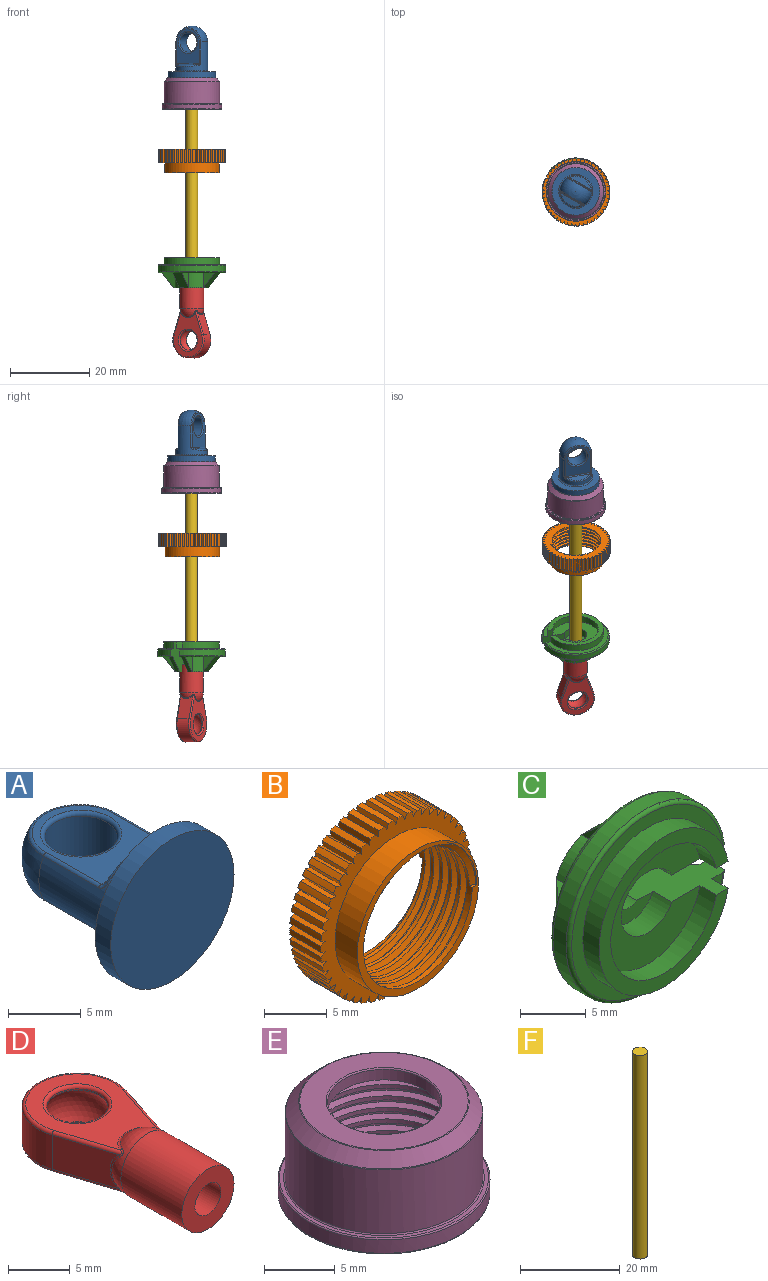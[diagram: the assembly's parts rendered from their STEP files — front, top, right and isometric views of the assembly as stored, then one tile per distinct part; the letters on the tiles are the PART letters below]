
ASSEMBLY  parts=6 mates=5
PART A: 27 faces, bbox 12x13x12 mm
  f0: revolved ~8x8mm, area 46.2mm2, adj f2,f6,f13
  f1: plane 8.65x6.57mm, normal (0,0,-1), area 27.5mm2, adj f2,f4,f15,f22,f23
  f2: bspline ~7.11x3.56mm, area 3.5mm2, adj f0,f1,f15,f23
  f3: bspline ~6.44x1.75mm, area 3.1mm2, adj f5,f8,f13,f24
  f4: cylinder r=0.3mm len=6.57mm, axis (-1,0,0), area 2.6mm2, adj f1,f5,f8,f24
  f5: bspline ~0.59x0.58mm, area 0.3mm2, adj f3,f4,f13,f23
  f6: bspline ~7.11x3.56mm, area 3.5mm2, adj f0,f7,f25,f26
  f7: plane 8.65x6.57mm, normal (0,0,1), area 27.5mm2, adj f6,f16,f20,f25,f26
  f8: plane 5.96x1.5mm, normal (0,0.98,-0.17), area 6.4mm2, adj f3,f4
  f9: plane 5.96x1.5mm, normal (0,0.98,0.17), area 6.4mm2, adj f16,f18
  f10: plane 12x12mm, normal (0,-1,0), area 113.1mm2, adj f11
  f11: cylinder r=6mm len=12mm, axis (0,-1,0), area 56.5mm2, adj f10,f12
  f12: plane 12x12mm, normal (0,1,0), area 55mm2, adj f11,f14
  f13: cylinder r=4mm len=8mm, axis (0,-1,0), area 77.5mm2, adj f0,f3,f5,f14,f15,f17,f18,f19
  f14: torus R=4.3mm, axis (0,-1,0), area 12.2mm2, adj f12,f13
  f15: cylinder r=0.3mm len=5.35mm, axis (0,-1,0), area 1.8mm2, adj f1,f2,f13,f24
  f16: cylinder r=0.3mm len=6.57mm, axis (-1,0,0), area 2.6mm2, adj f7,f9,f17,f19
  f17: bspline ~0.59x0.58mm, area 0.3mm2, adj f13,f16,f18,f26
  f18: bspline ~6.44x1.75mm, area 3.1mm2, adj f9,f13,f17,f19
  f19: bspline ~0.59x0.58mm, area 0.3mm2, adj f13,f16,f18,f25
  f20: torus R=2.8mm, axis (0,0,-1), area 7.7mm2, adj f7,f21
  f21: cylinder r=2.5mm len=5mm, axis (0,0,1), area 53.4mm2, adj f20,f22
  f22: torus R=2.8mm, axis (0,0,-1), area 7.7mm2, adj f1,f21
  f23: cylinder r=0.3mm len=5.35mm, axis (0,-1,0), area 1.8mm2, adj f1,f2,f5,f13
  f24: bspline ~0.59x0.58mm, area 0.3mm2, adj f3,f4,f13,f15
  f25: cylinder r=0.3mm len=5.35mm, axis (0,-1,0), area 1.8mm2, adj f6,f7,f13,f19
  f26: cylinder r=0.3mm len=5.35mm, axis (0,-1,0), area 1.8mm2, adj f6,f7,f13,f17
PART B: 160 faces, bbox 17.2x6.7x17.1 mm
  f0: cylinder r=6.15mm len=12.3mm, axis (0,-1,0), area 81.7mm2, adj f1,f2,f6,f7,f8,f9
  f1: bspline ~13.5x13.49mm, area 125.4mm2, adj f0,f2,f8,f10
  f2: plane 13.85x13.85mm, normal (0,-1,0), area 24mm2, adj f0,f1,f3,f9,f10
  f3: cylinder r=6.85mm len=13.7mm, axis (0,-1,0), area 107.6mm2, adj f2,f4
  f4: plane 17x16.99mm, normal (0,-1,0), area 73.3mm2, adj f3,f5,f11,f12,f13,f14,f15,f16
  f5: cylinder r=8.5mm len=3.5mm, axis (0,-1,0), area 2mm2, adj f4,f6,f107,f158
  f6: plane 17.15x17.14mm, normal (0,1,0), area 97.4mm2, adj f0,f5,f7,f8,f10,f11,f12,f13
  f7: bspline ~13.28x13.26mm, area 125.8mm2, adj f0,f6,f9,f10
  f8: plane 0.5x0.33mm, normal (0,0,-1), area 0.1mm2, adj f0,f1,f6,f10
  f9: plane 0.5x0.33mm, normal (0,0,1), area 0.1mm2, adj f0,f2,f7,f10
  f10: bspline ~13.5x13.49mm, area 62mm2, adj f1,f2,f6,f7,f8,f9
  f11: plane 3.5x0.54mm, normal (0.98,0,0.21), area 1.9mm2, adj f4,f6,f12,f157
  f12: plane 3.5x0.42mm, normal (-0.76,0,0.66), area 1.9mm2, adj f4,f6,f11,f156
  f13: plane 3.5x0.41mm, normal (-0.67,0,0.75), area 1.9mm2, adj f4,f6,f14,f155
  f14: plane 3.5x0.55mm, normal (1,0,0.09), area 1.9mm2, adj f4,f6,f13,f156
  f15: plane 3.5x0.46mm, normal (-0.57,0,0.82), area 1.9mm2, adj f4,f6,f16,f154
  f16: plane 3.5x0.55mm, normal (1,0,-0.04), area 1.9mm2, adj f4,f6,f15,f155
  f17: plane 3.5x0.49mm, normal (-0.46,0,0.89), area 1.9mm2, adj f4,f6,f18,f153
  f18: plane 3.5x0.55mm, normal (0.99,0,-0.16), area 1.9mm2, adj f4,f6,f17,f154
  f19: plane 3.5x0.52mm, normal (-0.35,0,0.94), area 1.9mm2, adj f4,f6,f20,f152
  f20: plane 3.5x0.53mm, normal (0.96,0,-0.29), area 1.9mm2, adj f4,f6,f19,f153
  f21: plane 3.5x0.54mm, normal (-0.23,0,0.97), area 1.9mm2, adj f4,f6,f22,f151
  f22: plane 3.5x0.51mm, normal (0.91,0,-0.4), area 1.9mm2, adj f4,f6,f21,f152
  f23: plane 3.5x0.55mm, normal (-0.1,0,0.99), area 1.9mm2, adj f4,f6,f24,f150
  f24: plane 3.5x0.48mm, normal (0.86,0,-0.52), area 1.9mm2, adj f4,f6,f23,f151
  f25: plane 3.5x0.56mm, normal (0.02,0,1), area 1.9mm2, adj f4,f6,f26,f149
  f26: plane 3.5x0.44mm, normal (0.79,0,-0.62), area 1.9mm2, adj f4,f6,f25,f150
  f27: plane 3.5x0.55mm, normal (0.15,0,0.99), area 1.9mm2, adj f4,f6,f28,f148
  f28: plane 3.5x0.4mm, normal (0.7,0,-0.71), area 1.9mm2, adj f4,f6,f27,f149
  f29: plane 3.5x0.53mm, normal (0.27,0,0.96), area 1.9mm2, adj f4,f6,f30,f147
  f30: plane 3.5x0.44mm, normal (0.61,0,-0.79), area 1.9mm2, adj f4,f6,f29,f148
  f31: plane 3.5x0.51mm, normal (0.39,0,0.92), area 1.9mm2, adj f4,f6,f32,f146
  f32: plane 3.5x0.48mm, normal (0.5,0,-0.86), area 1.9mm2, adj f4,f6,f31,f147
  f33: plane 3.5x0.48mm, normal (0.5,0,0.86), area 1.9mm2, adj f4,f6,f34,f145
  f34: plane 3.5x0.51mm, normal (0.39,0,-0.92), area 1.9mm2, adj f4,f6,f33,f146
  f35: plane 3.5x0.44mm, normal (0.61,0,0.79), area 1.9mm2, adj f4,f6,f36,f144
  f36: plane 3.5x0.53mm, normal (0.27,0,-0.96), area 1.9mm2, adj f4,f6,f35,f145
  f37: plane 3.5x0.4mm, normal (0.7,0,0.71), area 1.9mm2, adj f4,f6,f38,f143
  f38: plane 3.5x0.55mm, normal (0.15,0,-0.99), area 1.9mm2, adj f4,f6,f37,f144
  f39: plane 3.5x0.44mm, normal (0.79,0,0.62), area 1.9mm2, adj f4,f6,f40,f142
  f40: plane 3.5x0.56mm, normal (0.02,0,-1), area 1.9mm2, adj f4,f6,f39,f143
  f41: plane 3.5x0.48mm, normal (0.86,0,0.52), area 1.9mm2, adj f4,f6,f42,f141
  f42: plane 3.5x0.55mm, normal (-0.1,0,-0.99), area 1.9mm2, adj f4,f6,f41,f142
  f43: plane 3.5x0.51mm, normal (0.91,0,0.4), area 1.9mm2, adj f4,f6,f44,f140
  f44: plane 3.5x0.54mm, normal (-0.23,0,-0.97), area 1.9mm2, adj f4,f6,f43,f141
  f45: plane 3.5x0.53mm, normal (0.96,0,0.29), area 1.9mm2, adj f4,f6,f46,f139
  f46: plane 3.5x0.52mm, normal (-0.35,0,-0.94), area 1.9mm2, adj f4,f6,f45,f140
  f47: plane 3.5x0.55mm, normal (0.99,0,0.16), area 1.9mm2, adj f4,f6,f48,f138
  f48: plane 3.5x0.49mm, normal (-0.46,0,-0.89), area 1.9mm2, adj f4,f6,f47,f139
  f49: plane 3.5x0.55mm, normal (1,0,0.04), area 1.9mm2, adj f4,f6,f50,f137
  f50: plane 3.5x0.46mm, normal (-0.57,0,-0.82), area 1.9mm2, adj f4,f6,f49,f138
  f51: plane 3.5x0.55mm, normal (1,0,-0.09), area 1.9mm2, adj f4,f6,f52,f136
  f52: plane 3.5x0.41mm, normal (-0.67,0,-0.75), area 1.9mm2, adj f4,f6,f51,f137
  f53: plane 3.5x0.54mm, normal (0.98,0,-0.21), area 1.9mm2, adj f4,f6,f54,f135
  f54: plane 3.5x0.42mm, normal (-0.76,0,-0.66), area 1.9mm2, adj f4,f6,f53,f136
  f55: plane 3.5x0.52mm, normal (0.94,0,-0.33), area 1.9mm2, adj f4,f6,f56,f134
  f56: plane 3.5x0.46mm, normal (-0.83,0,-0.56), area 1.9mm2, adj f4,f6,f55,f135
  f57: plane 3.5x0.5mm, normal (0.89,0,-0.45), area 1.9mm2, adj f4,f6,f58,f133
  f58: plane 3.5x0.5mm, normal (-0.89,0,-0.45), area 1.9mm2, adj f4,f6,f57,f134
  f59: plane 3.5x0.46mm, normal (0.83,0,-0.56), area 1.9mm2, adj f4,f6,f60,f132
  f60: plane 3.5x0.52mm, normal (-0.94,0,-0.33), area 1.9mm2, adj f4,f6,f59,f133
  f61: plane 3.5x0.42mm, normal (0.76,0,-0.66), area 1.9mm2, adj f4,f6,f62,f131
  f62: plane 3.5x0.54mm, normal (-0.98,0,-0.21), area 1.9mm2, adj f4,f6,f61,f132
  f63: plane 3.5x0.41mm, normal (0.67,0,-0.75), area 1.9mm2, adj f4,f6,f64,f130
  f64: plane 3.5x0.55mm, normal (-1,0,-0.09), area 1.9mm2, adj f4,f6,f63,f131
  f65: plane 3.5x0.46mm, normal (0.57,0,-0.82), area 1.9mm2, adj f4,f6,f66,f129
  f66: plane 3.5x0.55mm, normal (-1,0,0.04), area 1.9mm2, adj f4,f6,f65,f130
  f67: plane 3.5x0.49mm, normal (0.46,0,-0.89), area 1.9mm2, adj f4,f6,f68,f128
  f68: plane 3.5x0.55mm, normal (-0.99,0,0.16), area 1.9mm2, adj f4,f6,f67,f129
  f69: plane 3.5x0.52mm, normal (0.35,0,-0.94), area 1.9mm2, adj f4,f6,f70,f127
  f70: plane 3.5x0.53mm, normal (-0.96,0,0.29), area 1.9mm2, adj f4,f6,f69,f128
  f71: plane 3.5x0.54mm, normal (0.23,0,-0.97), area 1.9mm2, adj f4,f6,f72,f126
  f72: plane 3.5x0.51mm, normal (-0.91,0,0.4), area 1.9mm2, adj f4,f6,f71,f127
  f73: plane 3.5x0.55mm, normal (0.1,0,-0.99), area 1.9mm2, adj f4,f6,f74,f125
  f74: plane 3.5x0.48mm, normal (-0.86,0,0.52), area 1.9mm2, adj f4,f6,f73,f126
  f75: plane 3.5x0.56mm, normal (-0.02,0,-1), area 1.9mm2, adj f4,f6,f76,f124
  f76: plane 3.5x0.44mm, normal (-0.79,0,0.62), area 1.9mm2, adj f4,f6,f75,f125
  f77: plane 3.5x0.55mm, normal (-0.15,0,-0.99), area 1.9mm2, adj f4,f6,f78,f123
  f78: plane 3.5x0.4mm, normal (-0.7,0,0.71), area 1.9mm2, adj f4,f6,f77,f124
  f79: plane 3.5x0.53mm, normal (-0.27,0,-0.96), area 1.9mm2, adj f4,f6,f80,f122
  f80: plane 3.5x0.44mm, normal (-0.61,0,0.79), area 1.9mm2, adj f4,f6,f79,f123
  f81: plane 3.5x0.51mm, normal (-0.39,0,-0.92), area 1.9mm2, adj f4,f6,f82,f121
  f82: plane 3.5x0.48mm, normal (-0.5,0,0.86), area 1.9mm2, adj f4,f6,f81,f122
  f83: plane 3.5x0.48mm, normal (-0.5,0,-0.86), area 1.9mm2, adj f4,f6,f84,f120
  f84: plane 3.5x0.51mm, normal (-0.39,0,0.92), area 1.9mm2, adj f4,f6,f83,f121
  f85: plane 3.5x0.44mm, normal (-0.61,0,-0.79), area 1.9mm2, adj f4,f6,f86,f119
  f86: plane 3.5x0.53mm, normal (-0.27,0,0.96), area 1.9mm2, adj f4,f6,f85,f120
  f87: plane 3.5x0.4mm, normal (-0.7,0,-0.71), area 1.9mm2, adj f4,f6,f88,f118
  f88: plane 3.5x0.55mm, normal (-0.15,0,0.99), area 1.9mm2, adj f4,f6,f87,f119
  f89: plane 3.5x0.44mm, normal (-0.79,0,-0.62), area 1.9mm2, adj f4,f6,f90,f117
  f90: plane 3.5x0.56mm, normal (-0.02,0,1), area 1.9mm2, adj f4,f6,f89,f118
  f91: plane 3.5x0.48mm, normal (-0.86,0,-0.52), area 1.9mm2, adj f4,f6,f92,f116
  f92: plane 3.5x0.55mm, normal (0.1,0,0.99), area 1.9mm2, adj f4,f6,f91,f117
  f93: plane 3.5x0.51mm, normal (-0.91,0,-0.4), area 1.9mm2, adj f4,f6,f94,f115
  f94: plane 3.5x0.54mm, normal (0.23,0,0.97), area 1.9mm2, adj f4,f6,f93,f116
  f95: plane 3.5x0.53mm, normal (-0.96,0,-0.29), area 1.9mm2, adj f4,f6,f96,f114
  f96: plane 3.5x0.52mm, normal (0.35,0,0.94), area 1.9mm2, adj f4,f6,f95,f115
  f97: plane 3.5x0.55mm, normal (-0.99,0,-0.16), area 1.9mm2, adj f4,f6,f98,f113
  f98: plane 3.5x0.49mm, normal (0.46,0,0.89), area 1.9mm2, adj f4,f6,f97,f114
  f99: plane 3.5x0.55mm, normal (-1,0,-0.04), area 1.9mm2, adj f4,f6,f100,f112
  f100: plane 3.5x0.46mm, normal (0.57,0,0.82), area 1.9mm2, adj f4,f6,f99,f113
  f101: plane 3.5x0.55mm, normal (-1,0,0.09), area 1.9mm2, adj f4,f6,f102,f111
  f102: plane 3.5x0.41mm, normal (0.67,0,0.75), area 1.9mm2, adj f4,f6,f101,f112
  f103: plane 3.5x0.54mm, normal (-0.98,0,0.21), area 1.9mm2, adj f4,f6,f104,f110
  f104: plane 3.5x0.42mm, normal (0.76,0,0.66), area 1.9mm2, adj f4,f6,f103,f111
  f105: plane 3.5x0.52mm, normal (-0.94,0,0.33), area 1.9mm2, adj f4,f6,f106,f109
  f106: plane 3.5x0.46mm, normal (0.83,0,0.56), area 1.9mm2, adj f4,f6,f105,f110
  f107: plane 3.5x0.5mm, normal (-0.89,0,0.45), area 1.9mm2, adj f4,f5,f6,f108
  f108: plane 3.5x0.5mm, normal (0.89,0,0.45), area 1.9mm2, adj f4,f6,f107,f109
  f109: cylinder r=8.5mm len=3.5mm, axis (0,-1,0), area 2mm2, adj f4,f6,f105,f108
  f110: cylinder r=8.5mm len=3.5mm, axis (0,-1,0), area 2mm2, adj f4,f6,f103,f106
  f111: cylinder r=8.5mm len=3.5mm, axis (0,-1,0), area 2mm2, adj f4,f6,f101,f104
  f112: cylinder r=8.5mm len=3.5mm, axis (0,-1,0), area 2mm2, adj f4,f6,f99,f102
  f113: cylinder r=8.5mm len=3.5mm, axis (0,-1,0), area 2mm2, adj f4,f6,f97,f100
  f114: cylinder r=8.5mm len=3.5mm, axis (0,-1,0), area 2mm2, adj f4,f6,f95,f98
  f115: cylinder r=8.5mm len=3.5mm, axis (0,-1,0), area 2mm2, adj f4,f6,f93,f96
  f116: cylinder r=8.5mm len=3.5mm, axis (0,-1,0), area 2mm2, adj f4,f6,f91,f94
  f117: cylinder r=8.5mm len=3.5mm, axis (0,-1,0), area 2mm2, adj f4,f6,f89,f92
  f118: cylinder r=8.5mm len=3.5mm, axis (0,-1,0), area 2mm2, adj f4,f6,f87,f90
  f119: cylinder r=8.5mm len=3.5mm, axis (0,-1,0), area 2mm2, adj f4,f6,f85,f88
  f120: cylinder r=8.5mm len=3.5mm, axis (0,-1,0), area 2mm2, adj f4,f6,f83,f86
  f121: cylinder r=8.5mm len=3.5mm, axis (0,-1,0), area 2mm2, adj f4,f6,f81,f84
  f122: cylinder r=8.5mm len=3.5mm, axis (0,-1,0), area 2mm2, adj f4,f6,f79,f82
  f123: cylinder r=8.5mm len=3.5mm, axis (0,-1,0), area 2mm2, adj f4,f6,f77,f80
  f124: cylinder r=8.5mm len=3.5mm, axis (0,-1,0), area 2mm2, adj f4,f6,f75,f78
  f125: cylinder r=8.5mm len=3.5mm, axis (0,-1,0), area 2mm2, adj f4,f6,f73,f76
  f126: cylinder r=8.5mm len=3.5mm, axis (0,-1,0), area 2mm2, adj f4,f6,f71,f74
  f127: cylinder r=8.5mm len=3.5mm, axis (0,-1,0), area 2mm2, adj f4,f6,f69,f72
  f128: cylinder r=8.5mm len=3.5mm, axis (0,-1,0), area 2mm2, adj f4,f6,f67,f70
  f129: cylinder r=8.5mm len=3.5mm, axis (0,-1,0), area 2mm2, adj f4,f6,f65,f68
  f130: cylinder r=8.5mm len=3.5mm, axis (0,-1,0), area 2mm2, adj f4,f6,f63,f66
  f131: cylinder r=8.5mm len=3.5mm, axis (0,-1,0), area 2mm2, adj f4,f6,f61,f64
  f132: cylinder r=8.5mm len=3.5mm, axis (0,-1,0), area 2mm2, adj f4,f6,f59,f62
  f133: cylinder r=8.5mm len=3.5mm, axis (0,-1,0), area 2mm2, adj f4,f6,f57,f60
  f134: cylinder r=8.5mm len=3.5mm, axis (0,-1,0), area 2mm2, adj f4,f6,f55,f58
  f135: cylinder r=8.5mm len=3.5mm, axis (0,-1,0), area 2mm2, adj f4,f6,f53,f56
  f136: cylinder r=8.5mm len=3.5mm, axis (0,-1,0), area 2mm2, adj f4,f6,f51,f54
  f137: cylinder r=8.5mm len=3.5mm, axis (0,-1,0), area 2mm2, adj f4,f6,f49,f52
  f138: cylinder r=8.5mm len=3.5mm, axis (0,-1,0), area 2mm2, adj f4,f6,f47,f50
  f139: cylinder r=8.5mm len=3.5mm, axis (0,-1,0), area 2mm2, adj f4,f6,f45,f48
  f140: cylinder r=8.5mm len=3.5mm, axis (0,-1,0), area 2mm2, adj f4,f6,f43,f46
  f141: cylinder r=8.5mm len=3.5mm, axis (0,-1,0), area 2mm2, adj f4,f6,f41,f44
  f142: cylinder r=8.5mm len=3.5mm, axis (0,-1,0), area 2mm2, adj f4,f6,f39,f42
  f143: cylinder r=8.5mm len=3.5mm, axis (0,-1,0), area 2mm2, adj f4,f6,f37,f40
  f144: cylinder r=8.5mm len=3.5mm, axis (0,-1,0), area 2mm2, adj f4,f6,f35,f38
  f145: cylinder r=8.5mm len=3.5mm, axis (0,-1,0), area 2mm2, adj f4,f6,f33,f36
  f146: cylinder r=8.5mm len=3.5mm, axis (0,-1,0), area 2mm2, adj f4,f6,f31,f34
  f147: cylinder r=8.5mm len=3.5mm, axis (0,-1,0), area 2mm2, adj f4,f6,f29,f32
  f148: cylinder r=8.5mm len=3.5mm, axis (0,-1,0), area 2mm2, adj f4,f6,f27,f30
  f149: cylinder r=8.5mm len=3.5mm, axis (0,-1,0), area 2mm2, adj f4,f6,f25,f28
  f150: cylinder r=8.5mm len=3.5mm, axis (0,-1,0), area 2mm2, adj f4,f6,f23,f26
  f151: cylinder r=8.5mm len=3.5mm, axis (0,-1,0), area 2mm2, adj f4,f6,f21,f24
  f152: cylinder r=8.5mm len=3.5mm, axis (0,-1,0), area 2mm2, adj f4,f6,f19,f22
  f153: cylinder r=8.5mm len=3.5mm, axis (0,-1,0), area 2mm2, adj f4,f6,f17,f20
  f154: cylinder r=8.5mm len=3.5mm, axis (0,-1,0), area 2mm2, adj f4,f6,f15,f18
  f155: cylinder r=8.5mm len=3.5mm, axis (0,-1,0), area 2mm2, adj f4,f6,f13,f16
  f156: cylinder r=8.5mm len=3.5mm, axis (0,-1,0), area 2mm2, adj f4,f6,f12,f14
  f157: cylinder r=8.5mm len=3.5mm, axis (0,-1,0), area 2mm2, adj f4,f6,f11,f159
  f158: plane 3.5x0.52mm, normal (0.94,0,0.33), area 1.9mm2, adj f4,f5,f6,f159
  f159: plane 3.5x0.46mm, normal (-0.83,0,0.56), area 1.9mm2, adj f4,f6,f157,f158
PART C: 34 faces, bbox 18.3x7.6x18.4 mm
  f0: plane 7.6x7.57mm, normal (0,0,1), area 29.6mm2, adj f2,f9,f10,f11,f12,f14,f15,f16
  f1: plane 7.6x7.57mm, normal (0,0,-1), area 29.6mm2, adj f2,f7,f9,f10,f11,f12,f14,f15
  f2: torus R=8.2mm, axis (0,1,0), area 23.7mm2, adj f0,f1,f15,f16
  f3: plane 3.93x3.8mm, normal (0,0,1), area 8.4mm2, adj f7,f9,f14,f29
  f4: plane 3.93x3.8mm, normal (0,0,-1), area 8.4mm2, adj f9,f14,f30,f32
  f5: plane 3.8x3.45mm, normal (-0.74,0.67,0), area 13.3mm2, adj f9,f14,f23,f24
  f6: plane 3.8x3.45mm, normal (0,0.67,-0.74), area 13.3mm2, adj f9,f14,f19,f20
  f7: plane 3.8x3.45mm, normal (0.74,0.67,0), area 5.4mm2, adj f1,f3,f9,f14
  f8: plane 3.8x3.45mm, normal (0,0.67,0.74), area 13.3mm2, adj f9,f14,f21,f22
  f9: plane 8.1x8.1mm, normal (0,1,0), area 27mm2, adj f0,f1,f3,f4,f5,f6,f7,f8
  f10: cylinder r=5.75mm len=11.5mm, axis (0,-1,0), area 58.8mm2, adj f0,f1,f11,f18
  f11: plane 11.5x11.37mm, normal (0,-1,0), area 71mm2, adj f0,f1,f10,f12
  f12: cylinder r=2.85mm len=5.7mm, axis (0,-1,0), area 30.6mm2, adj f0,f1,f11,f26
  f13: cylinder r=4.25mm len=3.8mm, axis (0,-1,0), area 15.3mm2, adj f9,f14,f19,f24
  f14: plane 16.4x16.31mm, normal (0,1,0), area 111.1mm2, adj f0,f1,f3,f4,f5,f6,f7,f8
  f15: cylinder r=8.5mm len=17mm, axis (0,-1,0), area 71.3mm2, adj f0,f1,f2,f28
  f16: plane 16.4x16.31mm, normal (0,-1,0), area 54.3mm2, adj f0,f1,f2,f17
  f17: cylinder r=7mm len=14mm, axis (0,-1,0), area 72.6mm2, adj f0,f1,f16,f18
  f18: plane 14x13.89mm, normal (0,-1,0), area 46.9mm2, adj f0,f1,f10,f17
  f19: plane 3.8x3.45mm, normal (-1,0,0), area 6.6mm2, adj f6,f9,f13,f14
  f20: plane 3.8x3.45mm, normal (1,0,0), area 6.6mm2, adj f6,f9,f14,f30
  f21: plane 3.8x3.45mm, normal (1,0,0), area 6.6mm2, adj f8,f9,f14,f29
  f22: plane 3.8x3.45mm, normal (-1,0,0), area 6.6mm2, adj f8,f9,f14,f31
  f23: plane 3.8x3.45mm, normal (0,0,1), area 6.6mm2, adj f5,f9,f14,f31
  f24: plane 3.8x3.45mm, normal (0,0,-1), area 6.6mm2, adj f5,f9,f13,f14
  f25: cylinder r=1.5mm len=3mm, axis (0,-1,0), area 12.9mm2, adj f0,f1,f26,f27
  f26: plane 5.7x5.41mm, normal (0,-1,0), area 14.8mm2, adj f0,f1,f12,f25
  f27: plane 5.7x5.41mm, normal (0,1,0), area 14.8mm2, adj f0,f1,f25,f33
  f28: torus R=8.2mm, axis (0,-1,0), area 23.7mm2, adj f0,f1,f14,f15
  f29: cylinder r=4.25mm len=3.8mm, axis (0,-1,0), area 11.1mm2, adj f3,f9,f14,f21
  f30: cylinder r=4.25mm len=3.8mm, axis (0,-1,0), area 11.1mm2, adj f4,f9,f14,f20
  f31: cylinder r=4.25mm len=3.8mm, axis (0,-1,0), area 15.3mm2, adj f9,f14,f22,f23
  f32: plane 3.8x3.45mm, normal (0.74,0.67,0), area 5.4mm2, adj f0,f4,f9,f14
  f33: cylinder r=2.85mm len=5.7mm, axis (0,-1,0), area 27.6mm2, adj f0,f1,f9,f27
PART D: 29 faces, bbox 9.7x19.9x6 mm
  f0: sphere r=3mm, area 26.4mm2, adj f2,f5,f6,f11,f22,f23,f24,f25
  f1: torus R=2.8mm, axis (0,0,1), area 7.7mm2, adj f14,f19
  f2: torus R=2.32mm, axis (-0.95,0.31,0), area 0.8mm2, adj f0,f21,f24,f25
  f3: cylinder r=0.3mm len=6.11mm, axis (-0.31,-0.95,0), area 2.9mm2, adj f7,f18,f21,f25
  f4: cylinder r=0.3mm len=6.11mm, axis (0.31,0.95,0), area 2.9mm2, adj f10,f19,f21,f24
  f5: torus R=2.37mm, axis (0,0,1), area 1.2mm2, adj f0,f18,f22,f25
  f6: torus R=2.37mm, axis (0,0,1), area 1.2mm2, adj f0,f19,f23,f24
  f7: torus R=4.2mm, axis (0,0,1), area 7.8mm2, adj f3,f8,f15,f18
  f8: cylinder r=0.3mm len=6.11mm, axis (-0.31,0.95,0), area 2.9mm2, adj f7,f18,f20,f22
  f9: cylinder r=0.3mm len=6.11mm, axis (0.31,-0.95,0), area 2.9mm2, adj f10,f19,f20,f23
  f10: torus R=4.2mm, axis (0,0,1), area 7.8mm2, adj f4,f9,f15,f19
  f11: torus R=2.32mm, axis (0.95,0.31,0), area 0.8mm2, adj f0,f20,f22,f23
  f12: cylinder r=2.5mm len=5mm, axis (0,0,1), area 2.1mm2, adj f16,f17
  f13: plane 6x6mm, normal (0,-1,0), area 21.2mm2, adj f26,f27
  f14: cylinder r=2.5mm len=5mm, axis (0,0,1), area 2.1mm2, adj f1,f17
  f15: cylinder r=4.5mm len=9mm, axis (0,0,-1), area 57.6mm2, adj f7,f10,f20,f21
  f16: torus R=2.8mm, axis (0,0,1), area 7.7mm2, adj f12,f18
  f17: sphere r=2.95mm, area 58.1mm2, adj f12,f14
  f18: plane 11.22x8.4mm, normal (0,0,1), area 44.7mm2, adj f3,f5,f7,f8,f16
  f19: plane 11.22x8.4mm, normal (0,0,-1), area 44.7mm2, adj f1,f4,f6,f9,f10
  f20: plane 5.74x3.4mm, normal (-0.95,-0.31,0), area 18.8mm2, adj f8,f9,f11,f15
  f21: plane 5.74x3.4mm, normal (0.95,-0.31,0), area 18.8mm2, adj f2,f3,f4,f15
  f22: bspline ~0.55x0.51mm, area 0.2mm2, adj f0,f5,f8,f11
  f23: bspline ~0.55x0.51mm, area 0.2mm2, adj f0,f6,f9,f11
  f24: bspline ~0.55x0.51mm, area 0.2mm2, adj f0,f2,f4,f6
  f25: bspline ~0.55x0.51mm, area 0.2mm2, adj f0,f2,f3,f5
  f26: cylinder r=3mm len=7mm, axis (0,-1,0), area 131.9mm2, adj f0,f13
  f27: cylinder r=1.5mm len=6mm, axis (0,-1,0), area 56.5mm2, adj f13,f28
  f28: plane 3x3mm, normal (0,-1,0), area 7.1mm2, adj f27
PART E: 26 faces, bbox 16.4x16.4x8.3 mm
  f0: bspline ~11.82x11.81mm, area 96.3mm2, adj f1,f2,f3,f4,f5,f6,f7,f19
  f1: cylinder r=5.5mm len=11mm, axis (0,0,-1), area 47mm2, adj f0,f2,f12,f21,f22
  f2: cylinder r=5.5mm len=11mm, axis (0,0,-1), area 12mm2, adj f0,f1,f3,f22
  f3: cylinder r=5.5mm len=11mm, axis (0,0,-1), area 12.8mm2, adj f0,f2,f4,f22
  f4: cylinder r=5.5mm len=11mm, axis (0,0,-1), area 12mm2, adj f0,f3,f5,f22
  f5: cylinder r=5.5mm len=11mm, axis (0,0,-1), area 11.3mm2, adj f0,f4,f6,f22
  f6: cylinder r=5.5mm len=11mm, axis (0,0,-1), area 13.6mm2, adj f0,f5,f7,f20,f22,f23
  f7: cylinder r=5.5mm len=4.92mm, axis (0,0,-1), area 0.5mm2, adj f0,f6,f23
  f8: torus R=4.1mm, axis (0,0,-1), area 4mm2, adj f9,f11
  f9: plane 11.92x11.92mm, normal (0,0,1), area 58.7mm2, adj f8,f18
  f10: cylinder r=7mm len=14mm, axis (0,0,-1), area 242.1mm2, adj f16,f17
  f11: cylinder r=4mm len=8mm, axis (0,0,-1), area 22.6mm2, adj f8,f12
  f12: plane 11x11mm, normal (0,0,-1), area 44.8mm2, adj f1,f11
  f13: cone r=7mm half-angle=45deg, axis (0,0,-1), area 54.4mm2, adj f17,f18
  f14: torus R=7.4mm, axis (0,0,1), area 7.4mm2, adj f23,f24
  f15: torus R=7.4mm, axis (0,0,-1), area 7.4mm2, adj f24,f25
  f16: torus R=7.1mm, axis (0,0,-1), area 6.9mm2, adj f10,f25
  f17: torus R=6.9mm, axis (0,0,1), area 3.4mm2, adj f10,f13
  f18: torus R=5.96mm, axis (0,0,-1), area 3mm2, adj f9,f13
  f19: bspline ~12.02x12.01mm, area 55.5mm2, adj f0,f20,f21,f22,f23
  f20: plane 0.42x0.32mm, normal (0,-1,0), area 0.1mm2, adj f6,f19,f22,f23
  f21: plane 0.65x0.42mm, normal (0,1,0), area 0.2mm2, adj f0,f1,f19,f22
  f22: bspline ~12.02x12.01mm, area 99.9mm2, adj f1,f2,f3,f4,f5,f6,f19,f20
  f23: plane 14.92x14.92mm, normal (0,0,-1), area 73.6mm2, adj f0,f6,f7,f14,f19,f20
  f24: cylinder r=7.5mm len=15mm, axis (0,0,-1), area 54.4mm2, adj f14,f15
  f25: plane 14.8x14.8mm, normal (0,0,1), area 13.7mm2, adj f15,f16
PART F: 3 faces, bbox 3x3x50 mm
  f0: plane 3x3mm, normal (0,0,-1), area 7.1mm2, adj f2
  f1: plane 3x3mm, normal (0,0,1), area 7.1mm2, adj f2
  f2: cylinder r=1.5mm len=50mm, axis (0,0,-1), area 471.2mm2, adj f0,f1
PLACE A rot(axis=(0.94,-0.25,-0.25),93.7deg) t=(0.12,-4,19.82)mm
PLACE B rot(axis=(0.18,0.7,0.7),159.3deg) t=(0.2,-4.22,-4.18)mm
PLACE C rot(axis=(-0.18,-0.7,0.7),159.3deg) t=(0.12,-4,-25.58)mm
PLACE D rot(axis=(-0.18,-0.7,0.7),159.3deg) t=(0.12,-4,-31.33)mm
PLACE E rot(axis=(0,0,1),150.6deg) t=(0.12,-4,11.82)mm
PLACE F rot(axis=(0,0,-1),119.4deg) t=(0.12,-4,-6.33)mm
MATE fastened E.f23 <-> B.f0  axis (0,0,-1) through (0.2,-4.22,11.82)mm
MATE fastened C.f2 <-> D.f26  axis (0,0,-1) through (0.12,-4,-31.33)mm
MATE slider F.f2 <-> E.f1  axis (0,0,-1) through (0.12,-4,-6.33)mm
MATE fastened A.f11 <-> E.f1  axis (0,0,-1) through (0.12,-4,19.82)mm
MATE fastened D.f26 <-> F.f2  axis (0,0,1) through (0.12,-4,-31.33)mm
